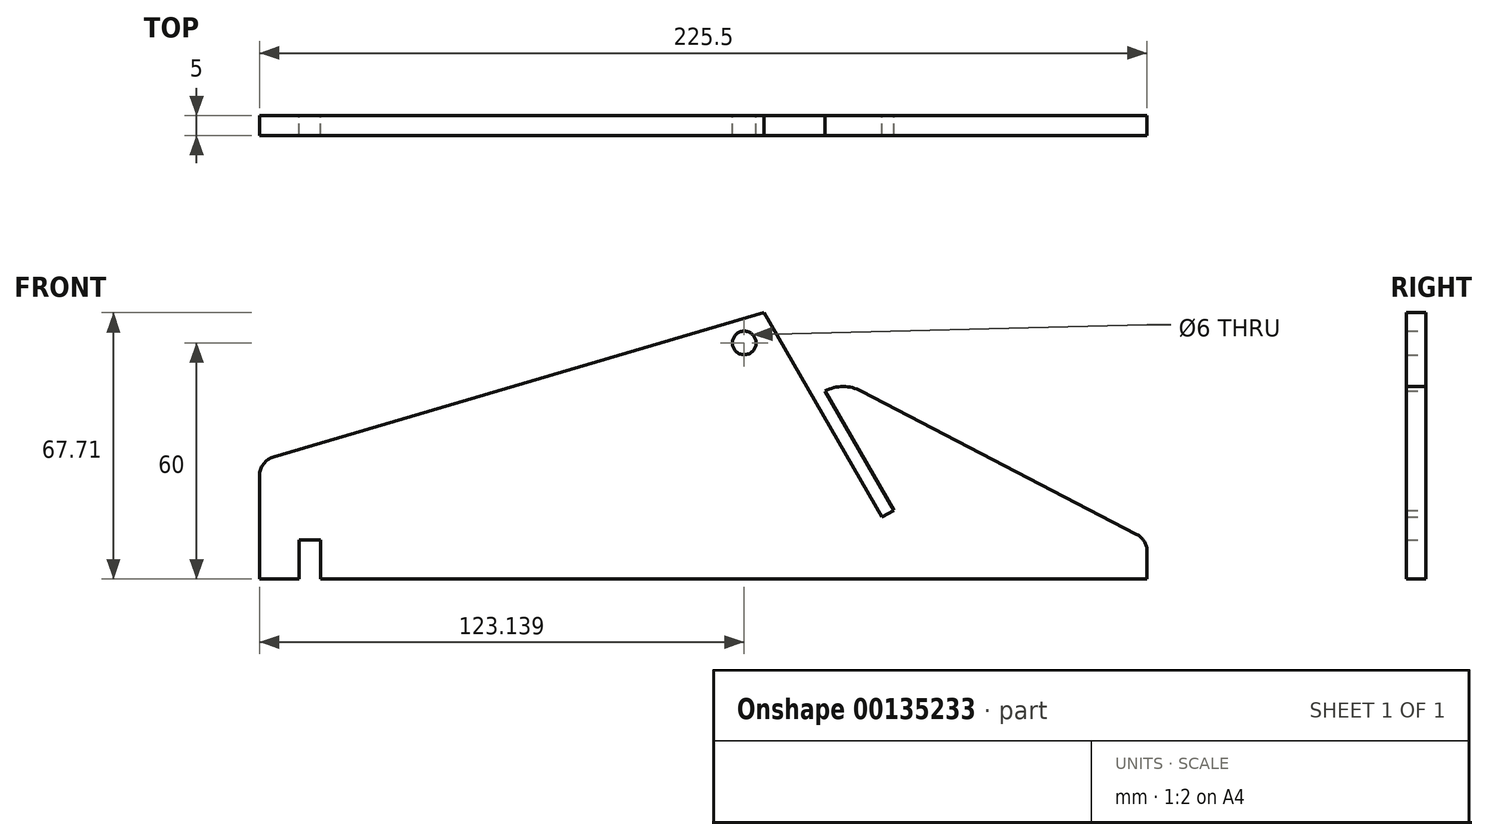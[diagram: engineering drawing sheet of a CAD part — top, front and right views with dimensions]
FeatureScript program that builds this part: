
annotation { "Feature Type Name" : "Feature", "Feature Type Description" : "" }
export const myFeature = defineFeature(function(context is Context, id is Id, definition is map)
    precondition{}
    {
        {
            var Q0;
            Q0=qCreatedBy(makeId("Front.planeOp"),FACE);
            var sketch = newSketch(context, id + "F0", { "sketchPlane" : qUnion([Q0])});
            skLineSegment(sketch, "E0", {"start": v(0, 0) * mm, "end": v(10, 0) * mm});
            skLineSegment(sketch, "E1", {"start": v(165.5, 0) * mm, "end": v(165.5, 20) * mm});
            skLineSegment(sketch, "E2", {"start": v(165.5, 20) * mm, "end": v(148, 50.31) * mm});
            skLineSegment(sketch, "E3", {"start": v(148, 50.31) * mm, "end": v(143.67, 47.81) * mm});
            skLineSegment(sketch, "E4", {"start": v(143.67, 47.81) * mm, "end": v(161.17, 17.5) * mm});
            skLineSegment(sketch, "E5", {"start": v(161.17, 17.5) * mm, "end": v(158.14, 15.75) * mm});
            skLineSegment(sketch, "E6", {"start": v(158.14, 15.75) * mm, "end": v(128.14, 67.71) * mm});
            skLineSegment(sketch, "E7", {"start": v(0, 30) * mm, "end": v(0, 0) * mm});
            skLineSegment(sketch, "E8", {"start": v(10, 0) * mm, "end": v(10, 10) * mm});
            skLineSegment(sketch, "E9", {"start": v(10, 10) * mm, "end": v(15.5, 10) * mm});
            skLineSegment(sketch, "E10", {"start": v(15.5, 10) * mm, "end": v(15.5, 0) * mm});
            skLineSegment(sketch, "E11.trimOffspring", {"start": v(15.5, 0) * mm, "end": v(165.5, 0) * mm});
            skLineSegment(sketch, "E12", {"start": v(0, 30) * mm, "end": v(128.14, 67.71) * mm});
            skLineSegment(sketch, "E13", {"start": v(165.5, 0) * mm, "end": v(225.5, 0) * mm});
            skLineSegment(sketch, "E14", {"start": v(225.5, 0) * mm, "end": v(225.5, 10) * mm});
            skLineSegment(sketch, "E15", {"start": v(225.5, 10) * mm, "end": v(148, 50.31) * mm});
            skCircle(sketch, "E16", {"center": v(123.14, 60) * mm, "radius": 3 * mm});
            skSolve(sketch);
        }
        {
            var Q0;
            Q0=makeQuery(id+"F0.imprint","IMPRINT",FACE,{"disambiguationData":[TD([[makeQuery(id+"F0.imprint","IMPRINT",EDGE,{"derivedFrom":sQuery(id+"F0.wireOp",EDGE,"E0")}),1.0]])]});
            var Q1;
            Q1=makeQuery(id+"F0.imprint","IMPRINT",FACE,{"disambiguationData":[TD([[makeQuery(id+"F0.imprint","IMPRINT",EDGE,{"derivedFrom":sQuery(id+"F0.wireOp",EDGE,"E1")}),-1.0]])]});
            extrude(context, id + "F1", {"entities" : qUnion([Q0, Q1]), "depth" : 5 * mm});
        }
        {
            var Q0;
            Q0=makeQuery(id+"F1.opExtrude","SWEPT_EDGE",EDGE,{"disambiguationData":[OSD([sQuery(id+"F0.wireOp",EDGE,"E1"),sQuery(id+"F0.wireOp",EDGE,"E2")])]});
            fillet(context, id + "F2", {"entities" : qUnion([Q0]), "radius" : 10 * mm, "tangentPropagation" : true, "allowEdgeOverflow" : false});
        }
        {
            var Q0;
            Q0=makeQuery(id+"F1.opExtrude","SWEPT_EDGE",EDGE,{"disambiguationData":[OSD([sQuery(id+"F0.wireOp",EDGE,"E14"),sQuery(id+"F0.wireOp",EDGE,"E15")])]});
            var Q1;
            Q1=makeQuery(id+"F1.opExtrude","SWEPT_EDGE",EDGE,{"disambiguationData":[OSD([sQuery(id+"F0.wireOp",EDGE,"E7"),sQuery(id+"F0.wireOp",EDGE,"E12")])]});
            fillet(context, id + "F3", {"entities" : qUnion([Q0, Q1]), "radius" : 5 * mm, "tangentPropagation" : true, "allowEdgeOverflow" : false});
        }
    });
